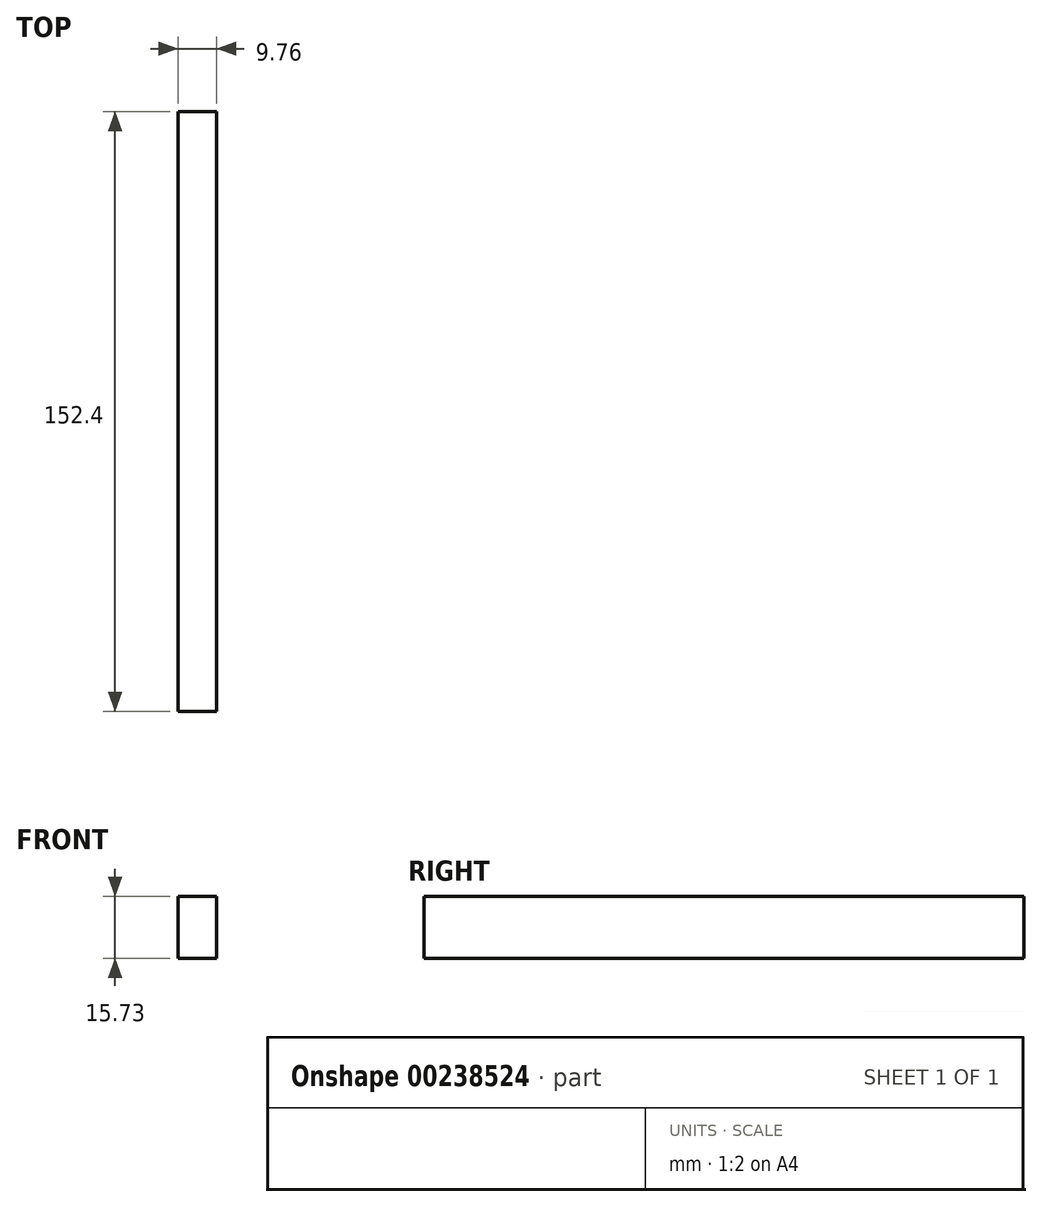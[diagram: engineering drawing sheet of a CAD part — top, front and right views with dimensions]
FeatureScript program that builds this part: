
annotation { "Feature Type Name" : "Feature", "Feature Type Description" : "" }
export const myFeature = defineFeature(function(context is Context, id is Id, definition is map)
    precondition{}
    {
        {
            var Q0;
            Q0=qCreatedBy(makeId("Front.planeOp"),FACE);
            var sketch = newSketch(context, id + "F0", { "sketchPlane" : qUnion([Q0])});
            skLineSegment(sketch, "E0.bottom", {"start": v(-5.22, 0) * mm, "end": v(4.54, 0) * mm});
            skLineSegment(sketch, "E0.top", {"start": v(-5.22, -15.73) * mm, "end": v(4.54, -15.73) * mm});
            skLineSegment(sketch, "E0.left", {"start": v(-5.22, 0) * mm, "end": v(-5.22, -15.73) * mm});
            skLineSegment(sketch, "E0.right", {"start": v(4.54, 0) * mm, "end": v(4.54, -15.73) * mm});
            skSolve(sketch);
        }
        {
            var Q0;
            Q0 = qSketchRegion(id + "F0", true);
            extrude(context, id + "F1", {"entities" : qUnion([Q0]), "depth" : 152.4 * mm});
        }
    });
